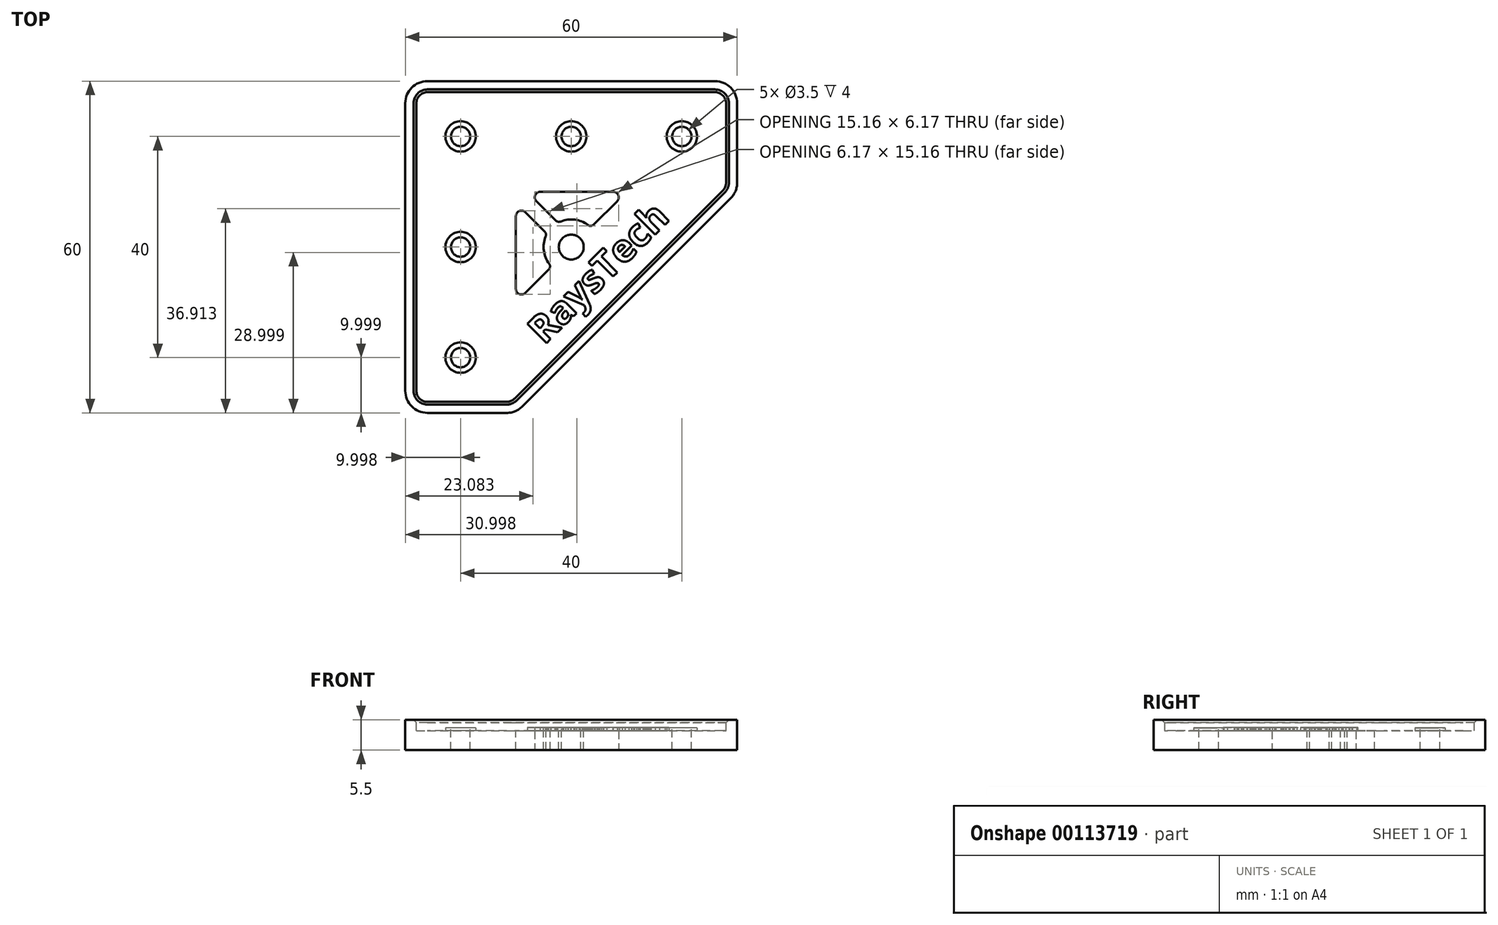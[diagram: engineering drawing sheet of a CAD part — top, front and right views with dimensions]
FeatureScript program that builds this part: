
annotation { "Feature Type Name" : "Feature", "Feature Type Description" : "" }
export const myFeature = defineFeature(function(context is Context, id is Id, definition is map)
    precondition{}
    {
        {
            var Q0;
            Q0=qCreatedBy(makeId("Top.planeOp"),FACE);
            var sketch = newSketch(context, id + "F0", { "sketchPlane" : qUnion([Q0])});
            skLineSegment(sketch, "E0", {"start": v(-45.73, 7.88) * mm, "end": v(14.27, 7.88) * mm});
            skLineSegment(sketch, "E1", {"start": v(14.27, 7.88) * mm, "end": v(14.27, -12.12) * mm});
            skLineSegment(sketch, "E2", {"start": v(14.27, -12.12) * mm, "end": v(-25.73, -52.12) * mm});
            skLineSegment(sketch, "E3", {"start": v(-25.73, -52.12) * mm, "end": v(-45.73, -52.12) * mm});
            skLineSegment(sketch, "E4", {"start": v(-45.73, -52.12) * mm, "end": v(-45.73, 7.88) * mm});
            skSolve(sketch);
        }
        {
            var Q0;
            Q0=makeQuery(id+"F0.imprint","IMPRINT",FACE,{"disambiguationData":[TD([[makeQuery(id+"F0.imprint","IMPRINT",EDGE,{"derivedFrom":sQuery(id+"F0.wireOp",EDGE,"E0")}),-1.0]])]});
            extrude(context, id + "F1", {"entities" : qUnion([Q0]), "depth" : 5.5 * mm});
        }
        {
            var Q0;
            Q0=makeQuery(id+"F1.opExtrude","SWEPT_EDGE",EDGE,{"disambiguationData":[OSD([sQuery(id+"F0.wireOp",EDGE,"E1"),sQuery(id+"F0.wireOp",EDGE,"E2")])]});
            var Q1;
            Q1=makeQuery(id+"F1.opExtrude","SWEPT_EDGE",EDGE,{"disambiguationData":[OSD([sQuery(id+"F0.wireOp",EDGE,"E0"),sQuery(id+"F0.wireOp",EDGE,"E1")])]});
            var Q2;
            Q2=makeQuery(id+"F1.opExtrude","SWEPT_EDGE",EDGE,{"disambiguationData":[OSD([sQuery(id+"F0.wireOp",EDGE,"E2"),sQuery(id+"F0.wireOp",EDGE,"E3")])]});
            var Q3;
            Q3=makeQuery(id+"F1.opExtrude","SWEPT_EDGE",EDGE,{"disambiguationData":[OSD([sQuery(id+"F0.wireOp",EDGE,"E3"),sQuery(id+"F0.wireOp",EDGE,"E4")])]});
            var Q4;
            Q4=makeQuery(id+"F1.opExtrude","SWEPT_EDGE",EDGE,{"disambiguationData":[OSD([sQuery(id+"F0.wireOp",EDGE,"E0"),sQuery(id+"F0.wireOp",EDGE,"E4")])]});
            fillet(context, id + "F2", {"entities" : qUnion([Q0, Q1, Q2, Q3, Q4]), "radius" : 4 * mm, "tangentPropagation" : true, "allowEdgeOverflow" : false});
        }
        {
            var Q0;
            Q0=makeQuery(id+"F1.opExtrude","CAP_FACE",FACE,{"disambiguationData":[OSD([sQuery(id+"F0.wireOp",EDGE,"E0"),sQuery(id+"F0.wireOp",EDGE,"E1"),sQuery(id+"F0.wireOp",EDGE,"E2"),sQuery(id+"F0.wireOp",EDGE,"E3"),sQuery(id+"F0.wireOp",EDGE,"E4"),sQuery(id+"F0.wireOp",EDGE,"C6Fx3dh9-c8in-fARx-cpzI-npJOqKGzg0Yl"),sQuery(id+"F0.wireOp",EDGE,"EsrDFDjG-3fY6-RK6S-8BCX-MYxAuXix4LG8"),sQuery(id+"F0.wireOp",EDGE,"29485572-baa4-49c2-8979-b70eeb0ac028.0.1.0"),sQuery(id+"F0.wireOp",EDGE,"29485572-baa4-49c2-8979-b70eeb0ac028.1.0.0")])],"isStart":false});
            shell(context, id + "F3", {"entities" : qUnion([Q0]), "thickness" : 2 * mm});
        }
        {
            var Q0;
            Q0=makeQuery(id+"F3.opShell","OFFSET_FACE",FACE,{"disambiguationData":[OSD([sQuery(id+"F0.wireOp",EDGE,"E0"),sQuery(id+"F0.wireOp",EDGE,"E1"),sQuery(id+"F0.wireOp",EDGE,"E2"),sQuery(id+"F0.wireOp",EDGE,"E3"),sQuery(id+"F0.wireOp",EDGE,"E4")])]});
            extrude(context, id + "F4", {"entities" : qUnion([Q0]), "operationType" : NewBodyOperationType.ADD, "depth" : 1.5 * mm});
        }
        {
            var Q0;
            Q0=makeQuery(id+"F4.opExtrude","CAP_FACE",FACE,{"disambiguationData":[OSD([sQuery(id+"F0.wireOp",EDGE,"E0"),sQuery(id+"F0.wireOp",EDGE,"E1"),sQuery(id+"F0.wireOp",EDGE,"E2"),sQuery(id+"F0.wireOp",EDGE,"E3"),sQuery(id+"F0.wireOp",EDGE,"E4")])],"isStart":false});
            var sketch = newSketch(context, id + "F5", { "sketchPlane" : qUnion([Q0])});
            skLineSegment(sketch, "E5", {"start": v(-25.73, -14.12) * mm, "end": v(-16.73, -23.12) * mm});
            skLineSegment(sketch, "E6", {"start": v(-16.73, -23.12) * mm, "end": v(-25.73, -32.12) * mm});
            skLineSegment(sketch, "E7", {"start": v(-25.73, -32.12) * mm, "end": v(-25.73, -14.12) * mm});
            skLineSegment(sketch, "E8", {"start": v(-23.73, -12.12) * mm, "end": v(-5.73, -12.12) * mm});
            skLineSegment(sketch, "E9", {"start": v(-5.73, -12.12) * mm, "end": v(-14.73, -21.12) * mm});
            skLineSegment(sketch, "E10", {"start": v(-14.73, -21.12) * mm, "end": v(-23.73, -12.12) * mm});
            skLineSegment(sketch, "E11", {"start": v(-14.73, -21.12) * mm, "end": v(-16.73, -23.12) * mm, "construction": true});
            skCircle(sketch, "E12", {"center": v(-15.73, -22.12) * mm, "radius": 5 * mm});
            skCircle(sketch, "E13", {"center": v(-15.73, -22.12) * mm, "radius": 2.25 * mm});
            skCircle(sketch, "E14", {"center": v(-15.73, -2.12) * mm, "radius": 1.75 * mm});
            skCircle(sketch, "E15", {"center": v(-35.73, -2.12) * mm, "radius": 1.75 * mm});
            skCircle(sketch, "E16.0.1.0", {"center": v(-35.73, -22.12) * mm, "radius": 1.75 * mm});
            skCircle(sketch, "E16.0.2.0", {"center": v(-35.73, -42.12) * mm, "radius": 1.75 * mm});
            skLineSegment(sketch, "E16.direction1", {"start": v(-35.73, -2.12) * mm, "end": v(-10.73, -2.12) * mm, "construction": true});
            skLineSegment(sketch, "E16.direction2", {"start": v(-35.73, -2.12) * mm, "end": v(-35.73, -22.12) * mm, "construction": true});
            skCircle(sketch, "E17.1.0.0", {"center": v(4.27, -2.12) * mm, "radius": 1.75 * mm});
            skLineSegment(sketch, "E17.direction1", {"start": v(-15.73, -2.12) * mm, "end": v(4.27, -2.12) * mm, "construction": true});
            skSolve(sketch);
        }
        {
            var Q0;
            Q0=makeQuery(id+"F5.imprint","IMPRINT",FACE,{"disambiguationData":[TD([[makeQuery(id+"F5.imprint","IMPRINT",EDGE,{"derivedFrom":sQuery(id+"F5.wireOp",EDGE,"E15")}),1.0]])]});
            var Q1;
            Q1=makeQuery(id+"F5.imprint","IMPRINT",FACE,{"disambiguationData":[TD([[makeQuery(id+"F5.imprint","IMPRINT",EDGE,{"derivedFrom":sQuery(id+"F5.wireOp",EDGE,"E16.0.1.0")}),1.0]])]});
            var Q2;
            Q2=makeQuery(id+"F5.imprint","IMPRINT",FACE,{"disambiguationData":[TD([[makeQuery(id+"F5.imprint","IMPRINT",EDGE,{"derivedFrom":sQuery(id+"F5.wireOp",EDGE,"E16.0.2.0")}),1.0]])]});
            var Q3;
            Q3=makeQuery(id+"F5.imprint","IMPRINT",FACE,{"disambiguationData":[TD([[makeQuery(id+"F5.imprint","IMPRINT",EDGE,{"derivedFrom":sQuery(id+"F5.wireOp",EDGE,"E14")}),1.0]])]});
            var Q4;
            Q4=makeQuery(id+"F5.imprint","IMPRINT",FACE,{"disambiguationData":[TD([[makeQuery(id+"F5.imprint","IMPRINT",EDGE,{"derivedFrom":sQuery(id+"F5.wireOp",EDGE,"E17.1.0.0")}),1.0]])]});
            var Q5;
            {var subQ0=sQuery(id+"F5.wireOp",EDGE,"E7");Q5=makeQuery(id+"F5.imprint","IMPRINT",FACE,{"disambiguationData":[TD([[makeQuery(id+"F5.imprint","IMPRINT",EDGE,{"derivedFrom":subQ0}),-1.0]])]});}
            var Q6;
            {var subQ0=sQuery(id+"F5.wireOp",EDGE,"E8");Q6=makeQuery(id+"F5.imprint","IMPRINT",FACE,{"disambiguationData":[TD([[makeQuery(id+"F5.imprint","IMPRINT",EDGE,{"derivedFrom":subQ0}),-1.0]])]});}
            var Q7;
            {var subQ6=sQuery(id+"F5.wireOp",EDGE,"E6");var subQ7=sQuery(id+"F5.wireOp",EDGE,"E5");var subQ8=makeQuery(id+"F5.imprint","INTERSECT",VERTEX,{"derivedFrom":[subQ7,subQ6]});Q7=makeQuery(id+"F5.imprint","IMPRINT",FACE,{"disambiguationData":[TD([[makeQuery(id+"F5.imprint","IMPRINT",EDGE,{"disambiguationData":[TD([[subQ8,1.0]])],"derivedFrom":subQ7}),1.0]])]});}
            var Q8;
            {var subQ0=sQuery(id+"F5.wireOp",EDGE,"E10");var subQ1=sQuery(id+"F5.wireOp",EDGE,"E9");var subQ2=makeQuery(id+"F5.imprint","INTERSECT",VERTEX,{"derivedFrom":[subQ1,subQ0]});Q8=makeQuery(id+"F5.imprint","IMPRINT",FACE,{"disambiguationData":[TD([[makeQuery(id+"F5.imprint","IMPRINT",EDGE,{"disambiguationData":[TD([[subQ2,1.0]])],"derivedFrom":subQ1}),-1.0]])]});}
            var Q9;
            {var subQ0=sQuery(id+"F5.wireOp",EDGE,"E6");var subQ1=sQuery(id+"F5.wireOp",EDGE,"E5");var subQ2=makeQuery(id+"F5.imprint","INTERSECT",VERTEX,{"derivedFrom":[subQ1,subQ0]});Q9=makeQuery(id+"F5.imprint","IMPRINT",FACE,{"disambiguationData":[TD([[makeQuery(id+"F5.imprint","IMPRINT",EDGE,{"disambiguationData":[TD([[subQ2,1.0]])],"derivedFrom":subQ1}),-1.0]])]});}
            extrude(context, id + "F6", {"entities" : qUnion([Q0, Q1, Q2, Q3, Q4, Q5, Q6, Q7, Q8, Q9]), "operationType" : NewBodyOperationType.REMOVE, "oppositeDirection" : true, "depth" : 25 * mm});
        }
        {
            var Q0;
            Q0=makeQuery(id+"F6.boolean.opBoolean","COPY",EDGE,{"derivedFrom":makeQuery(id+"F6.opExtrude","SWEPT_EDGE",EDGE,{"disambiguationData":[OSD([sQuery(id+"F5.wireOp",EDGE,"E8"),sQuery(id+"F5.wireOp",EDGE,"E10")])]})});
            var Q1;
            Q1=makeQuery(id+"F6.boolean.opBoolean","COPY",EDGE,{"derivedFrom":makeQuery(id+"F6.opExtrude","SWEPT_EDGE",EDGE,{"disambiguationData":[OSD([sQuery(id+"F5.wireOp",EDGE,"E5"),sQuery(id+"F5.wireOp",EDGE,"E7")])]})});
            var Q2;
            Q2=makeQuery(id+"F6.boolean.opBoolean","COPY",EDGE,{"derivedFrom":makeQuery(id+"F6.opExtrude","SWEPT_EDGE",EDGE,{"disambiguationData":[OSD([sQuery(id+"F5.wireOp",EDGE,"E8"),sQuery(id+"F5.wireOp",EDGE,"E9")])]})});
            var Q3;
            Q3=makeQuery(id+"F6.boolean.opBoolean","COPY",EDGE,{"derivedFrom":makeQuery(id+"F6.opExtrude","SWEPT_EDGE",EDGE,{"disambiguationData":[OSD([sQuery(id+"F5.wireOp",EDGE,"E6"),sQuery(id+"F5.wireOp",EDGE,"E7")])]})});
            fillet(context, id + "F7", {"entities" : qUnion([Q0, Q1, Q2, Q3]), "radius" : 1 * mm, "tangentPropagation" : true, "allowEdgeOverflow" : false});
        }
        {
            var Q0;
            Q0=makeQuery(id+"F6.boolean.opBoolean","COPY",EDGE,{"derivedFrom":makeQuery(id+"F6.opExtrude","SWEPT_EDGE",EDGE,{"disambiguationData":[OSD([sQuery(id+"F5.wireOp",EDGE,"E9"),sQuery(id+"F5.wireOp",EDGE,"E12")])]})});
            var Q1;
            Q1=makeQuery(id+"F6.boolean.opBoolean","COPY",EDGE,{"derivedFrom":makeQuery(id+"F6.opExtrude","SWEPT_EDGE",EDGE,{"disambiguationData":[OSD([sQuery(id+"F5.wireOp",EDGE,"E10"),sQuery(id+"F5.wireOp",EDGE,"E12")])]})});
            var Q2;
            Q2=makeQuery(id+"F6.boolean.opBoolean","COPY",EDGE,{"derivedFrom":makeQuery(id+"F6.opExtrude","SWEPT_EDGE",EDGE,{"disambiguationData":[OSD([sQuery(id+"F5.wireOp",EDGE,"E6"),sQuery(id+"F5.wireOp",EDGE,"E12")])]})});
            var Q3;
            Q3=makeQuery(id+"F6.boolean.opBoolean","COPY",EDGE,{"derivedFrom":makeQuery(id+"F6.opExtrude","SWEPT_EDGE",EDGE,{"disambiguationData":[OSD([sQuery(id+"F5.wireOp",EDGE,"E5"),sQuery(id+"F5.wireOp",EDGE,"E12")])]})});
            fillet(context, id + "F8", {"entities" : qUnion([Q0, Q1, Q2, Q3]), "radius" : 0.8 * mm, "tangentPropagation" : true, "allowEdgeOverflow" : false});
        }
        {
            var Q0;
            Q0=makeQuery(id+"F4.opExtrude","CAP_FACE",FACE,{"disambiguationData":[OSD([sQuery(id+"F0.wireOp",EDGE,"E0"),sQuery(id+"F0.wireOp",EDGE,"E1"),sQuery(id+"F0.wireOp",EDGE,"E2"),sQuery(id+"F0.wireOp",EDGE,"E3"),sQuery(id+"F0.wireOp",EDGE,"E4")])],"isStart":false});
            var sketch = newSketch(context, id + "F9", { "sketchPlane" : qUnion([Q0])});
            skText(sketch, "E18", { "text": "RaysTech", "fontName": "OpenSans-Bold.ttf"});
            const initialGuessF9  = {"E18": [-0.02063, -0.03995, 0.7071, 0.7071, 0.005]};
            skSetInitialGuess(sketch, initialGuessF9);
            skSolve(sketch);
        }
        {
            var Q0;
            Q0 = qSketchRegion(id + "F9", true);
            extrude(context, id + "F10", {"entities" : qUnion([Q0]), "operationType" : NewBodyOperationType.ADD, "depth" : 0.6 * mm});
        }
        {
            var Q0;
            {var subQ0=sQuery(id+"F0.wireOp",EDGE,"E0");Q0=makeQuery(id+"F3.opShell","OFFSET_EDGE",EDGE,{"disambiguationData":[OSD([subQ0]),TDD([makeQuery(id+"F1.opExtrude","CAP_EDGE",EDGE,{"disambiguationData":[OSD([subQ0])],"isStart":false})])]});}
            chamfer(context, id + "F11", {"entities" : qUnion([Q0]), "width" : 0.5 * mm, "tangentPropagation" : true});
        }
        {
            var Q0;
            {var subQ5=sQuery(id+"F0.wireOp",EDGE,"E4");var subQ6=sQuery(id+"F0.wireOp",EDGE,"E0");var subQ7=sQuery(id+"F0.wireOp",EDGE,"E3");var subQ8=sQuery(id+"F0.wireOp",EDGE,"E2");var subQ10=sQuery(id+"F0.wireOp",EDGE,"E1");Q0=makeQuery(id+"F10.boolean.opBoolean","SPLIT",FACE,{"disambiguationData":[TD([makeQuery(id+"F3.opShell","OFFSET_FACE",FACE,{"disambiguationData":[OSD([subQ6])]})])],"derivedFrom":makeQuery(id+"F4.opExtrude","CAP_FACE",FACE,{"disambiguationData":[OSD([subQ6,subQ10,subQ8,subQ7,subQ5])],"isStart":false})});}
            var sketch = newSketch(context, id + "F12", { "sketchPlane" : qUnion([Q0])});
            skCircle(sketch, "E19", {"center": v(-35.73, -2.12) * mm, "radius": 2.75 * mm});
            skCircle(sketch, "E20.0.1.0", {"center": v(-35.73, -22.12) * mm, "radius": 2.75 * mm});
            skCircle(sketch, "E20.0.2.0", {"center": v(-35.73, -42.12) * mm, "radius": 2.75 * mm});
            skLineSegment(sketch, "E20.direction1", {"start": v(-35.73, -2.12) * mm, "end": v(-10.73, -2.12) * mm, "construction": true});
            skLineSegment(sketch, "E20.direction2", {"start": v(-35.73, -2.12) * mm, "end": v(-35.73, -22.12) * mm, "construction": true});
            skCircle(sketch, "E21.1.0.0", {"center": v(-15.73, -2.12) * mm, "radius": 2.75 * mm});
            skCircle(sketch, "E21.2.0.0", {"center": v(4.27, -2.12) * mm, "radius": 2.75 * mm});
            skLineSegment(sketch, "E21.direction1", {"start": v(-35.73, -2.12) * mm, "end": v(-15.73, -2.12) * mm, "construction": true});
            skSolve(sketch);
        }
        {
            var Q0;
            Q0=makeQuery(id+"F12.imprint","IMPRINT",FACE,{"disambiguationData":[TD([[makeQuery(id+"F12.imprint","IMPRINT",EDGE,{"derivedFrom":sQuery(id+"F12.wireOp",EDGE,"E19")}),1.0]])]});
            var Q1;
            Q1=makeQuery(id+"F12.imprint","IMPRINT",FACE,{"disambiguationData":[TD([[makeQuery(id+"F12.imprint","IMPRINT",EDGE,{"derivedFrom":sQuery(id+"F12.wireOp",EDGE,"E20.0.1.0")}),1.0]])]});
            var Q2;
            Q2=makeQuery(id+"F12.imprint","IMPRINT",FACE,{"disambiguationData":[TD([[makeQuery(id+"F12.imprint","IMPRINT",EDGE,{"derivedFrom":sQuery(id+"F12.wireOp",EDGE,"E20.0.2.0")}),1.0]])]});
            var Q3;
            Q3=makeQuery(id+"F12.imprint","IMPRINT",FACE,{"disambiguationData":[TD([[makeQuery(id+"F12.imprint","IMPRINT",EDGE,{"derivedFrom":sQuery(id+"F12.wireOp",EDGE,"E21.1.0.0")}),1.0]])]});
            var Q4;
            Q4=makeQuery(id+"F12.imprint","IMPRINT",FACE,{"disambiguationData":[TD([[makeQuery(id+"F12.imprint","IMPRINT",EDGE,{"derivedFrom":sQuery(id+"F12.wireOp",EDGE,"E21.2.0.0")}),1.0]])]});
            extrude(context, id + "F13", {"entities" : qUnion([Q0, Q1, Q2, Q3, Q4]), "operationType" : NewBodyOperationType.ADD, "depth" : 0.5 * mm});
        }
    });
